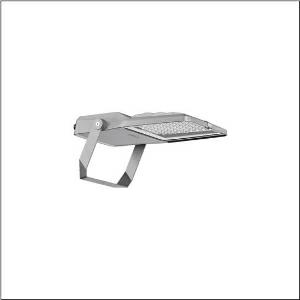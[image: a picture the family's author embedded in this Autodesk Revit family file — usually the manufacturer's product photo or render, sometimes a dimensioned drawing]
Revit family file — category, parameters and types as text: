
# Revit family: floodlight_fl_21_mini___pl33t_5xa7775b2f1a_fedb
name_source: partatom
category: Lighting Fixtures
units: mm (PartAtom-declared; Revit-internal decimal feet)

## family parameters
Cut with Voids When Loaded = No
Host = Face
Light Source = No
Part Type = Normal
Room Calculation Point = No
Round Connector Dimension = Use Diameter
Shared = No

## types (1)
- --- (1 x LED, 6150 lm, 45.7 W, 3000K)
    Apparent Load = 46 VA
    CIE Flux Codes = 26 75 99 100 100
    Color Rendering = 70
    Color Temperature = 3000K
    Default Elevation = 1800 mm
    Description = Floodlight FL 21 mini, floodlight, primary light control with lens, of PMMA, primary optical cover: protective disc, of toughened safety glass, transparent, light distribution: PL33T, light emission: direct distribution, installation type: surface-mounted, LED, High Power LED, rated luminous flux: 6.150lm, luminous efficacy: 135lm/W, light colour: 730, colour temperature: 3000K, control gear: Smart Interface (Zhaga), control: flexible luminous flux parameterisation, time-dependent luminous flux control, constant luminous flux control, overheat protection, pre-setting: logarithmic dimming characteristic, with terminal, 6-pole, mains connection: 220..240V, AC, 50/60Hz, start of lifetime: 46W, end of service life: 48W, reduction: 22W, luminaire housing, of diecast aluminium, powder-coated, Siteco® metallic grey (DB 702S), corrosivity category C5 mid according to DIN EN ISO 12944, suitable for swimming pools, chlorine-resistant, sealing non-destructively replaceable, mounting bracket, of steel, galvanised, powder-coated, Siteco® metallic grey (DB 702S), Smart Interface above, protection rating (complete): IP66, insulation class (complete): insulation class II (safety insulation), certification: CE, ENEC, VDE, protection symbol: D, impact resistance: IK08, permissible operating ambient temperature: -40..+40°C, permissible operating ambient temperature for outdoor applications: -40..+50°C, standard: DIN EN 12944, LABS conformity tested according to VDMA 24364:2018-05, packaging unit: 1 piece

Light Distribution: PL33T
    Height = 70 mm
    Lamp = 1 x LED
    Lamp Light Flux = 6150 lm
    Lamp Power = 45.7 W
    Lamp count = 1
    Length = 485 mm
    Luminous efficacy = 135 lm/W
    Manufacturer = Siteco
    ModVariant = No
    Model = 5XA7775B2F1A
    Number of Poles = 1
    OnlyDefault = Yes
    Power Factor = 1
    Product Name = Floodlight FL 21 mini | PL33T
    Product group = floodlight | pylon annexe
    ProductGroupID = 6200
    Protection Class = Protection class II
    Protection Degree = IP 66
    RLX_Detail_Level = 1
    RLX_Emergency_Light_Flux = 0 lm
    RLX_Emergency_Type = 0
    RLX_Emergency_Type_DB = No
    RlxData = <blob elided: 95893 chars, md5=6b01061f>
    Socket = socket
    Standby Power = 0 W
    System Light Flux = 6150 lm
    System Power = 46 W
    Type Comments = factory setting: luminous flux: 100 % | dim-lin: 254 | 463 mA
    Type Image = l_1006845.jpg
    URL = http://relux.com
    VarID = @adj_148708
    Voltage = 0 V
    Weight = 0.00 kg
    Width = 337 mm

## geometry (parser evidence)
native form markers: Blend x4, Sweep x13
no freeform markers — native parametric forms only
